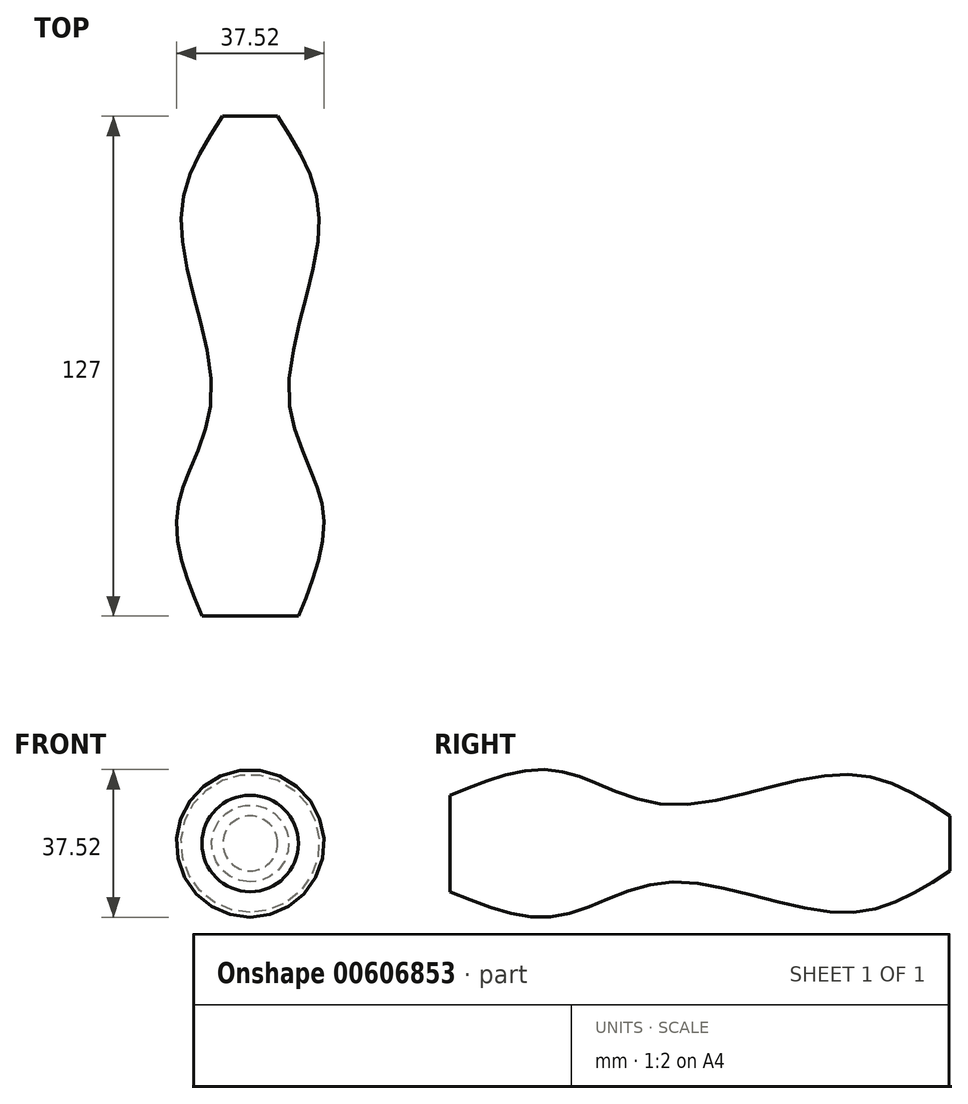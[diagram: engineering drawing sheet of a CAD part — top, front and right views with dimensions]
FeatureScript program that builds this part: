
annotation { "Feature Type Name" : "Feature", "Feature Type Description" : "" }
export const myFeature = defineFeature(function(context is Context, id is Id, definition is map)
    precondition{}
    {
        {
            var Q0;
            Q0=qCreatedBy(makeId("Right.planeOp"),FACE);
            var sketch = newSketch(context, id + "F0", { "sketchPlane" : qUnion([Q0])});
            skLineSegment(sketch, "E0", {"start": v(0, 0) * mm, "end": v(127, 0) * mm});
            skLineSegment(sketch, "E1", {"start": v(127, 0) * mm, "end": v(127, 6.97) * mm});
            skLineSegment(sketch, "E2", {"start": v(0, 0) * mm, "end": v(0, 12.26) * mm});
            skFitSpline(sketch, "E3", {"points": [v(0, 12.26) * mm, v(27.03, 18.5) * mm, v(55.39, 9.85) * mm, v(100.09, 17.54) * mm, v(127, 6.97) * mm], "startDerivative": vector(119.41, 48.87) * mm, "endDerivative": vector(102.95, -67.58) * mm});
            skSolve(sketch);
        }
        {
            var Q0;
            Q0=makeQuery(id+"F0.imprint","IMPRINT",FACE,{"disambiguationData":[TD([[makeQuery(id+"F0.imprint","IMPRINT",EDGE,{"derivedFrom":sQuery(id+"F0.wireOp",EDGE,"E0")}),1.0]])]});
            var Q1;
            Q1=sQuery(id+"F0.wireOp",EDGE,"E0");
            revolve(context, id + "F1", {"entities" : qUnion([Q0]), "axis" : qUnion([Q1]), "revolveType" : RevolveType.FULL});
        }
    });
